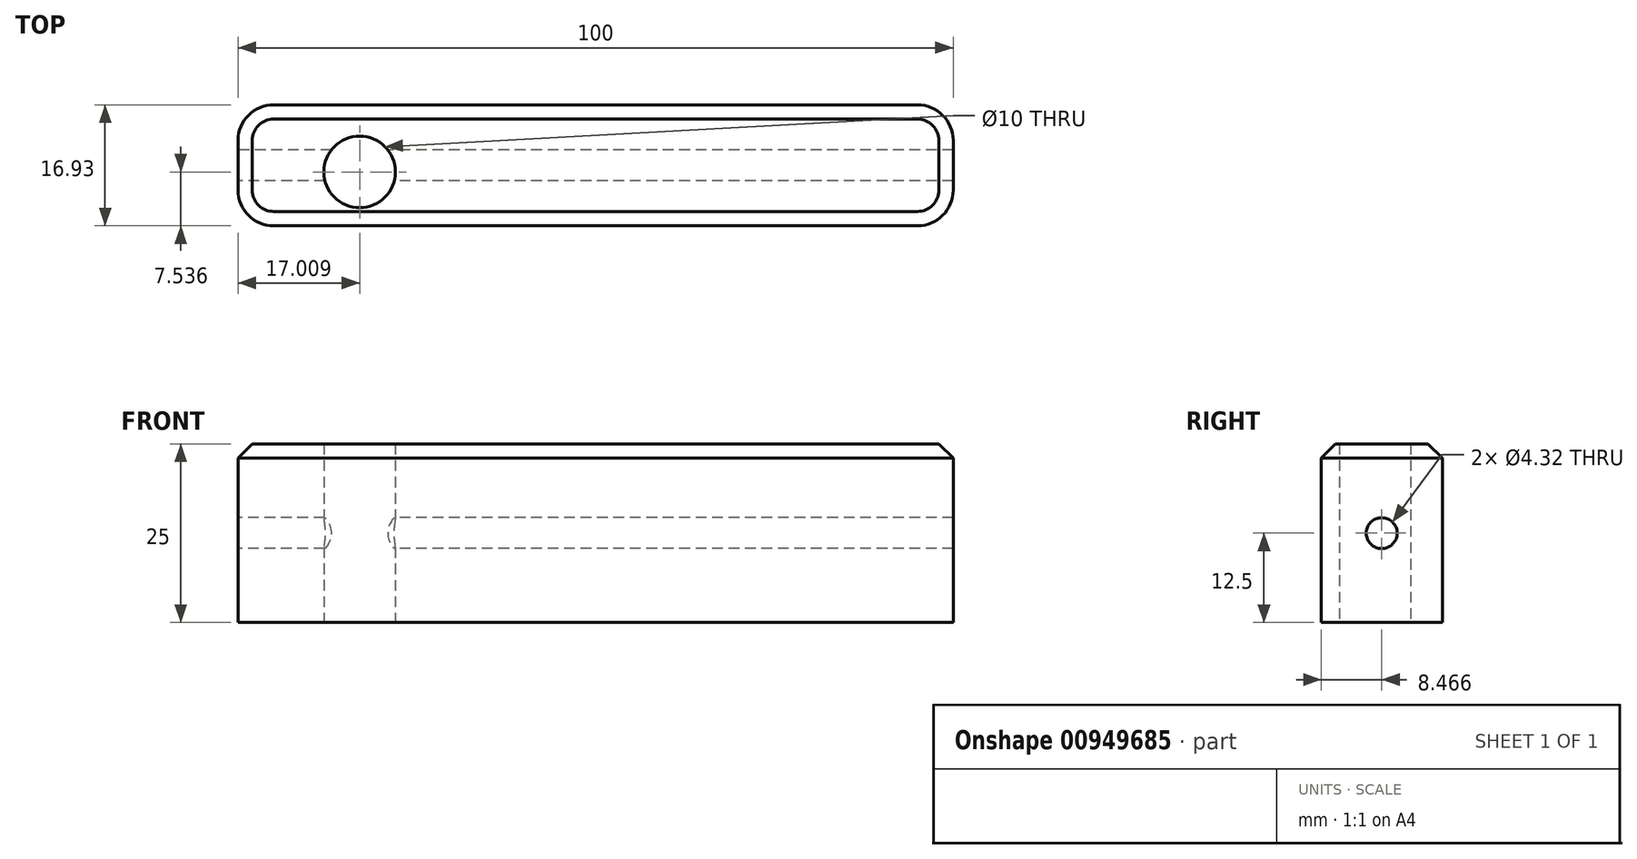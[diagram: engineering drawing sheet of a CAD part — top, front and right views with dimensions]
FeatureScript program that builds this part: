
annotation { "Feature Type Name" : "Feature", "Feature Type Description" : "" }
export const myFeature = defineFeature(function(context is Context, id is Id, definition is map)
    precondition{}
    {
        {
            var Q0;
            Q0=qCreatedBy(makeId("Top.planeOp"),FACE);
            var sketch = newSketch(context, id + "F0", { "sketchPlane" : qUnion([Q0])});
            skLineSegment(sketch, "E0.bottom", {"start": v(0, 0) * mm, "end": v(0, 0) * mm});
            skLineSegment(sketch, "E0.top", {"start": v(0, 0) * mm, "end": v(0, 0) * mm});
            skLineSegment(sketch, "E0.left", {"start": v(0, 0) * mm, "end": v(0, 0) * mm});
            skLineSegment(sketch, "E0.right", {"start": v(0, 0) * mm, "end": v(0, 0) * mm});
            skLineSegment(sketch, "E1.bottom", {"start": v(-45, 16.93) * mm, "end": v(45, 16.93) * mm});
            skLineSegment(sketch, "E1.top", {"start": v(-45, 0) * mm, "end": v(45, 0) * mm});
            skLineSegment(sketch, "E1.left", {"start": v(-50, 11.93) * mm, "end": v(-50, 5) * mm});
            skLineSegment(sketch, "E1.right", {"start": v(50, 11.93) * mm, "end": v(50, 5) * mm});
            skPoint(sketch, "E2.visualSharp", {"position": v(-50, 16.93) * mm});
            skArc(sketch, "E2.filletArc", {"start": v(-45, 16.93) * mm, "mid": v(-48.54, 15.47) * mm, "end": v(-50, 11.93) * mm});
            skPoint(sketch, "E3.visualSharp", {"position": v(50, 16.93) * mm});
            skArc(sketch, "E3.filletArc", {"start": v(50, 11.93) * mm, "mid": v(48.54, 15.47) * mm, "end": v(45, 16.93) * mm});
            skPoint(sketch, "E4.visualSharp", {"position": v(50, 0) * mm});
            skArc(sketch, "E4.filletArc", {"start": v(45, 0) * mm, "mid": v(48.54, 1.46) * mm, "end": v(50, 5) * mm});
            skPoint(sketch, "E5.visualSharp", {"position": v(-50, 0) * mm});
            skArc(sketch, "E5.filletArc", {"start": v(-50, 5) * mm, "mid": v(-48.54, 1.46) * mm, "end": v(-45, 0) * mm});
            skCircle(sketch, "E6", {"center": v(-33, 7.54) * mm, "radius": 5 * mm});
            skSolve(sketch);
        }
        {
            var Q0;
            Q0 = qSketchRegion(id + "F0", true);
            extrude(context, id + "F1", {"entities" : qUnion([Q0]), "depth" : 25 * mm, "offsetDistance" : 25 * mm});
        }
        {
            var Q0;
            Q0=makeQuery(id+"F1.opExtrude","SWEPT_FACE",FACE,{"disambiguationData":[OSD([sQuery(id+"F0.wireOp",EDGE,"E1.left")])]});
            var sketch = newSketch(context, id + "F2", { "sketchPlane" : qUnion([Q0])});
            skCircle(sketch, "E7", {"center": v(-8.47, 12.5) * mm, "radius": 2.16 * mm});
            skLineSegment(sketch, "E8", {"start": v(-11.93, 25) * mm, "end": v(-5, 0) * mm});
            skSolve(sketch);
        }
        {
            var Q0;
            Q0 = qSketchRegion(id + "F2", true);
            extrude(context, id + "F3", {"entities" : qUnion([Q0]), "operationType" : NewBodyOperationType.REMOVE, "endBound" : BoundingType.THROUGH_ALL, "oppositeDirection" : true, "depth" : 25 * mm, "offsetDistance" : 25 * mm});
        }
        {
            var Q0;
            Q0=makeQuery(id+"F1.opExtrude","CAP_EDGE",EDGE,{"disambiguationData":[OSD([sQuery(id+"F0.wireOp",EDGE,"E1.bottom")])],"isStart":false});
            chamfer(context, id + "F4", {"entities" : qUnion([Q0]), "width" : 2 * mm, "tangentPropagation" : true});
        }
    });
